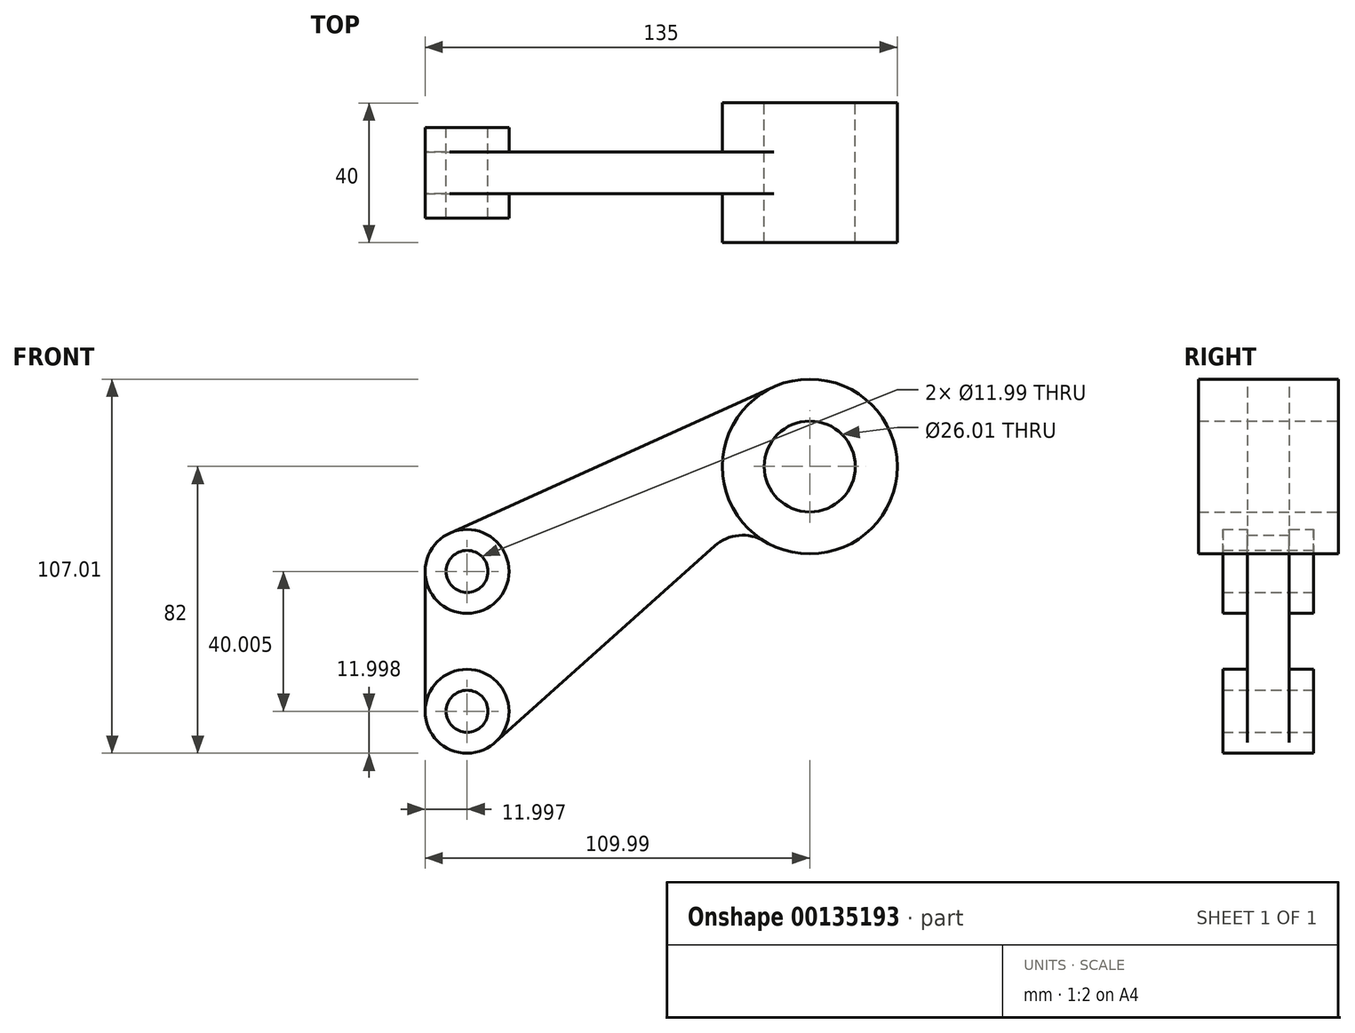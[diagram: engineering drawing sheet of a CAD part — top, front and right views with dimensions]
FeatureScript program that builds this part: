
annotation { "Feature Type Name" : "Feature", "Feature Type Description" : "" }
export const myFeature = defineFeature(function(context is Context, id is Id, definition is map)
    precondition{}
    {
        {
            var Q0;
            Q0=qCreatedBy(makeId("Front.planeOp"),FACE);
            var sketch = newSketch(context, id + "F0", { "sketchPlane" : qUnion([Q0])});
            skCircle(sketch, "E0", {"center": v(0, 0) * mm, "radius": 13 * mm});
            skCircle(sketch, "E1", {"center": v(0, 0) * mm, "radius": 25 * mm});
            skLineSegment(sketch, "E2", {"start": v(-10.3, 22.79) * mm, "end": v(-102.93, -19.06) * mm});
            skCircle(sketch, "E3", {"center": v(-98, -30) * mm, "radius": 6 * mm});
            skCircle(sketch, "E4", {"center": v(-98, -30) * mm, "radius": 12 * mm});
            skCircle(sketch, "E5", {"center": v(-98, -70) * mm, "radius": 6 * mm});
            skCircle(sketch, "E6", {"center": v(-98, -70) * mm, "radius": 12 * mm});
            skLineSegment(sketch, "E7", {"start": v(-110, -30) * mm, "end": v(-110, -70) * mm});
            skArc(sketch, "E8", {"start": v(-12.95, -21.4) * mm, "mid": v(-20.27, -19.71) * mm, "end": v(-27.15, -22.71) * mm});
            skLineSegment(sketch, "E9", {"start": v(-90, -78.95) * mm, "end": v(-27.15, -22.71) * mm});
            skSolve(sketch);
        }
        {
            var Q0;
            {var subQ4=sQuery(id+"F0.wireOp",EDGE,"E2");Q0=makeQuery(id+"F0.imprint","IMPRINT",FACE,{"disambiguationData":[TD([[makeQuery(id+"F0.imprint","IMPRINT",EDGE,{"derivedFrom":subQ4}),1.0]])]});}
            extrude(context, id + "F1", {"entities" : qUnion([Q0]), "endBound" : BoundingType.SYMMETRIC, "depth" : 12 * mm});
        }
        {
            var Q0;
            Q0=makeQuery(id+"F0.imprint","IMPRINT",FACE,{"disambiguationData":[TD([[makeQuery(id+"F0.imprint","IMPRINT",EDGE,{"derivedFrom":sQuery(id+"F0.wireOp",EDGE,"E3")}),-1.0]])]});
            var Q1;
            Q1=makeQuery(id+"F0.imprint","IMPRINT",FACE,{"disambiguationData":[TD([[makeQuery(id+"F0.imprint","IMPRINT",EDGE,{"derivedFrom":sQuery(id+"F0.wireOp",EDGE,"E5")}),-1.0]])]});
            extrude(context, id + "F2", {"entities" : qUnion([Q0, Q1]), "operationType" : NewBodyOperationType.ADD, "endBound" : BoundingType.SYMMETRIC, "depth" : 26 * mm});
        }
        {
            var Q0;
            Q0=makeQuery(id+"F0.imprint","IMPRINT",FACE,{"disambiguationData":[TD([[makeQuery(id+"F0.imprint","IMPRINT",EDGE,{"derivedFrom":sQuery(id+"F0.wireOp",EDGE,"E0")}),-1.0]])]});
            extrude(context, id + "F3", {"entities" : qUnion([Q0]), "operationType" : NewBodyOperationType.ADD, "endBound" : BoundingType.SYMMETRIC, "depth" : 40 * mm});
        }
    });
